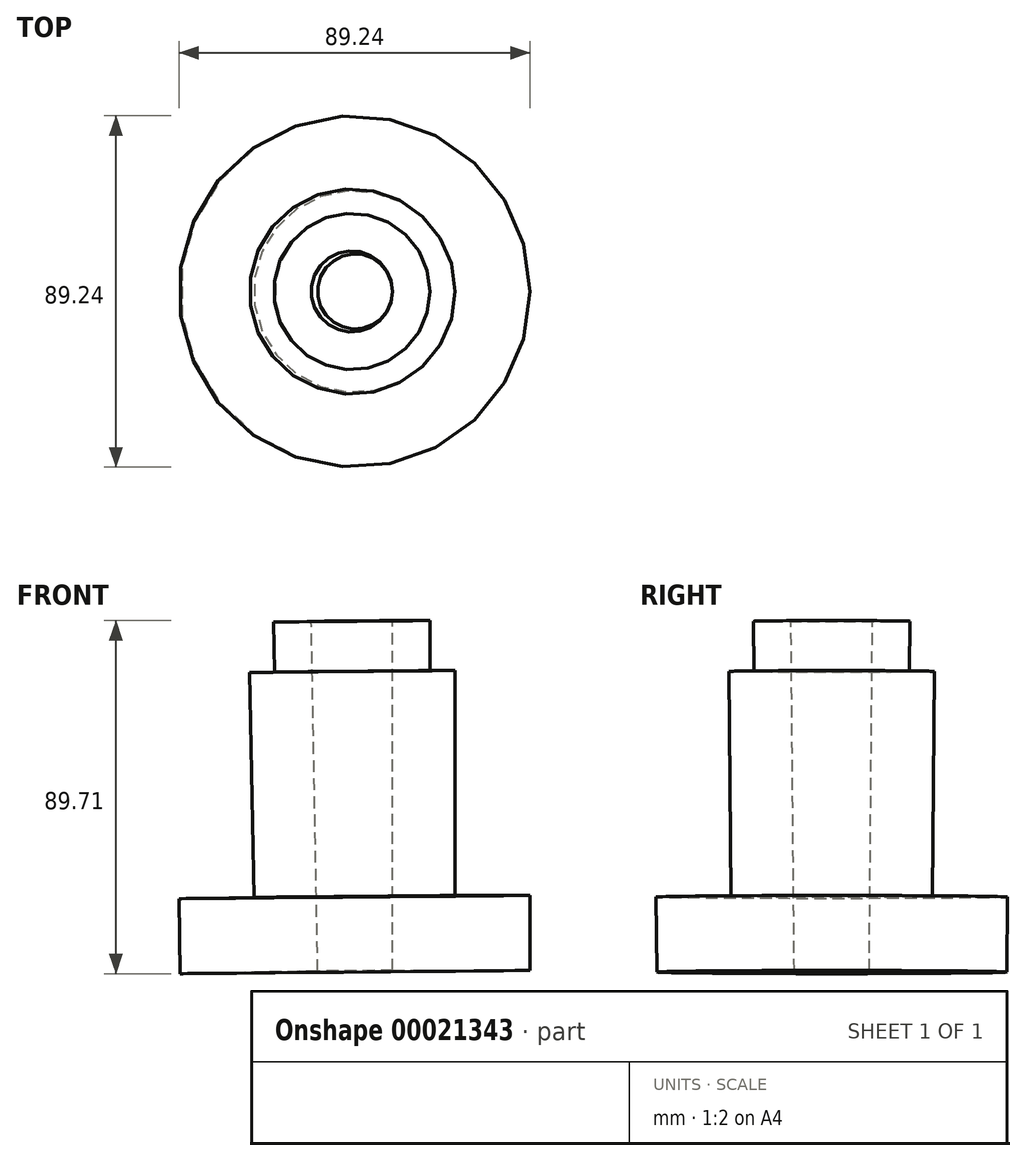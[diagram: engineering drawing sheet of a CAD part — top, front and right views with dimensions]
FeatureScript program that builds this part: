
annotation { "Feature Type Name" : "Feature", "Feature Type Description" : "" }
export const myFeature = defineFeature(function(context is Context, id is Id, definition is map)
    precondition{}
    {
        {
            var Q0;
            Q0=qCreatedBy(makeId("Front.planeOp"),FACE);
            var sketch = newSketch(context, id + "F0", { "sketchPlane" : qUnion([Q0])});
            skLineSegment(sketch, "E0", {"start": v(-44.45, -42.83) * mm, "end": v(0, -42.83) * mm});
            skLineSegment(sketch, "E1", {"start": v(-34.93, 46.07) * mm, "end": v(-25.4, 46.07) * mm});
            skLineSegment(sketch, "E2", {"start": v(-25.4, 46.07) * mm, "end": v(-25.4, 33.37) * mm});
            skLineSegment(sketch, "E3", {"start": v(-25.4, 33.37) * mm, "end": v(-19.05, 33.37) * mm});
            skLineSegment(sketch, "E4", {"start": v(-19.05, 33.37) * mm, "end": v(-19.05, -23.78) * mm});
            skLineSegment(sketch, "E5", {"start": v(-19.05, -23.78) * mm, "end": v(0, -23.78) * mm});
            skLineSegment(sketch, "E6", {"start": v(0, -23.78) * mm, "end": v(0, -42.83) * mm});
            skPoint(sketch, "E7", {"position": v(-34.93, 46.07) * mm});
            skLineSegment(sketch, "E8", {"start": v(-34.93, 46.07) * mm, "end": v(-34.93, -42.83) * mm});
            skLineSegment(sketch, "E9", {"start": v(-34.93, 46.07) * mm, "end": v(-45.26, 46.07) * mm});
            skLineSegment(sketch, "E10", {"start": v(-45.26, 46.07) * mm, "end": v(-44.45, -42.83) * mm});
            skSolve(sketch);
        }
        {
            var Q0;
            {var subQ1=sQuery(id+"F0.wireOp",EDGE,"cf03975f-66bc-4771-87a0-c7f4b4a50331");Q0=makeQuery(id+"F0.imprint","IMPRINT",FACE,{"disambiguationData":[TD([[makeQuery(id+"F0.imprint","IMPRINT",EDGE,{"derivedFrom":subQ1}),1.0]])]});}
            var Q1;
            {var subQ4=sQuery(id+"F0.wireOp",EDGE,"E1");Q1=makeQuery(id+"F0.imprint","IMPRINT",FACE,{"disambiguationData":[TD([[makeQuery(id+"F0.imprint","IMPRINT",EDGE,{"derivedFrom":subQ4}),-1.0]])]});}
            var Q2;
            Q2=sQuery(id+"F0.wireOp",EDGE,"E10");
            revolve(context, id + "F1", {"entities" : qUnion([Q0, Q1]), "axis" : qUnion([Q2]), "revolveType" : RevolveType.FULL});
        }
    });
